# Revit family: Hager-VOLTA-Flush_mounted-IP30-With_Cover-With_DIN-Hosted-DE-de
name_source: partatom
category: Electrical Equipment
units: mm (PartAtom-declared; Revit-internal decimal feet)

## family parameters
Cut with Voids When Loaded = No
Host = Face
Maintain Annotation Orientation = Yes
Panel Configuration = Two Columns, Circuits Across
Part Type = Panelboard
Room Calculation Point = No
Round Connector Dimension = Use Diameter
Shared = No

## types (64) — shared parameters
BC_MODEL_ID = 1547151
BC_OBJECT_ID = 513474
BC_OBJECT_VERSION = #2
Code hager = ADD-EC000214_EU
EF000003 - Montageart = Unterputz
EF000008 - Breite = 348 mm  [stored 1.14173 ft]
EF000024 - UV-beständig = No
EF000116 - RAL-Nummer = 9010
EF001062 - EMV-Ausführung = No
EF001134 - DIN-Schiene = Yes
EF002950 - Breite in Teilungseinheiten = 12
EF005474 - Schutzart (IP) = IP30
EF006306 - Mit Schloss = No
ETIM class code = EC000214
ETIM class name = Small distribution board
HG000002-Mit tür = Yes
HG000003-Bereich = VOLTA
HG000005-Dicke = 2 mm  [stored 0.00656168 ft]
HG000006-Flush mounted = Yes
HG000009-Doppelflügeligen Tür = No
HG000010-Asymmetrische Türen = No
HG000012-Türschwenkwinkel = 90.00°
HG000013-Tür links = No
HG000014-Tür rechts = Yes
HG000015-Sichtbarkeit der Türöffnung = Yes
HG000016-3D-Türsichtbarkeit = Yes
HG000017-Distanz zwischen den Polen = 18 mm  [stored 0.0590551 ft]
HG000060-RAL-number = 9010
HG000099-Onfly Template ID-de-DE = 507532
HGEF0002950-Breite in Teilungseinheiten = 12
Manufacturer = Hager
Name = VOLTA-Flush_mounted-IP30-With_Cover-With_DIN-DE
Name BIM&CO = Electricity
Name hager = ADD_Enclosures_EC000214
Uniformat = Low Tension Service & Dist.
Uniformat code = D501001
zero-valued in all types: Default Elevation, EF001131 - Innentiefe, HG000007-Anzahl der leeren Spalten

## per-type parameters (varying)
| type | BC_VARIANT_ID | EF000007 - Farbe | EF000040 - Höhe | EF000049 - Tiefe | EF000118 - Mit Montageplatte | EF000218 - Einbautiefe | EF000266 - Anzahl der Reihen | EF000332 - Einbauhöhe | EF000846 - Einbaubreite | EF001088 - Anbaumöglichkeit | EF004462 - Art der Schließung | EF006244 - Transparenter Deckel/Tür | EF009212 - Ausführung Deckel | EF015776 - Erdungsklemmenblock | EF015777 - Neutralleiterklemmenblock | EF015941 - Signaldurchlassende Tür | HG000001-Anzahl der Spalten | HG000004-Herstellerreferenz | HG000008-Anzahl der leeren Reihen | HG000011-Leere Reihen von unten | HGEF000266-Anzahl der Reihen |
| VOLTA-Flush_mounted_W348_H356_D98_12_Modular_Spacing-VU12AT | 1174115 | weiß | 356 mm  [stored 1.16798 ft] | 98 mm  [stored 0.321522 ft] | No | 89 mm  [stored 0.291995 ft] | 1 | 321 mm  [stored 1.05315 ft] | 315 mm | Yes | sonstige | No | mit Ausschnitt | Yes | Yes | No | 1 | VU12AT | 0 | No | 1 |
| VOLTA-Flush_mounted_W348_H356_D94_12_Modular_Spacing-VU12DKN | 1174116 | weiß | 356 mm  [stored 1.16798 ft] | 94 mm  [stored 0.308399 ft] | No | 90 mm  [stored 0.295276 ft] | 1 | 340 mm  [stored 1.11549 ft] | 335 mm  [stored 1.09908 ft] | Yes | sonstige | No | mit Ausschnitt | No | No | No | 1 | VU12DKN | 0 | No | 1 |
| VOLTA-Flush_mounted_W348_H356_D94_12_Modular_Spacing-VU12EP | 1174117 | weiß | 356 mm  [stored 1.16798 ft] | 94 mm  [stored 0.308399 ft] | No | 90 mm  [stored 0.295276 ft] | 1 | 321 mm  [stored 1.05315 ft] | 335 mm  [stored 1.09908 ft] | Yes | sonstige | No | mit Ausschnitt | Yes | No | No | 1 | VU12EP | 0 | No | 1 |
| VOLTA-Flush_mounted_W348_H356_D94_12_Modular_Spacing-VU12ET | 1174118 | weiß | 356 mm  [stored 1.16798 ft] | 94 mm  [stored 0.308399 ft] | No | 90 mm  [stored 0.295276 ft] | 1 | 321 mm  [stored 1.05315 ft] | 335 mm  [stored 1.09908 ft] | Yes | sonstige | Yes | mit Ausschnitt | Yes | No | No | 1 | VU12ET | 0 | No | 1 |
| VOLTA-Flush_mounted_W348_H356_D98_12_Modular_Spacing-VU12LN | 1174119 | weiß | 356 mm  [stored 1.16798 ft] | 98 mm  [stored 0.321522 ft] | Yes | 89 mm  [stored 0.291995 ft] | 1 | 321 mm  [stored 1.05315 ft] | 315 mm | Yes | sonstige | No | mit Ausschnitt | Yes | No | No | 1 | VU12LN | 0 | No | 1 |
| VOLTA-Flush_mounted_W348_H356_D98_12_Modular_Spacing-VU12NA | 1174120 | weiß | 356 mm  [stored 1.16798 ft] | 98 mm  [stored 0.321522 ft] | No | 89 mm  [stored 0.291995 ft] | 1 | 321 mm  [stored 1.05315 ft] | 315 mm | Yes | sonstige | No | mit Ausschnitt | Yes | No | No | 1 | VU12NA | 0 | No | 1 |
| VOLTA-Flush_mounted_W348_H356_D98_12_Modular_Spacing-VU12NC | 1174121 |  | 356 mm  [stored 1.16798 ft] | 98 mm  [stored 0.321522 ft] | No | 89 mm  [stored 0.291995 ft] | 1 | 321 mm  [stored 1.05315 ft] | 315 mm | No |  | No |  | No | No | No | 1 | VU12NC | 0 | No | 1 |
| VOLTA-Flush_mounted_W348_H356_D94_12_Modular_Spacing-VU12NG | 1174122 | weiß | 356 mm  [stored 1.16798 ft] | 94 mm  [stored 0.308399 ft] | No | 90 mm  [stored 0.295276 ft] | 1 | 340 mm  [stored 1.11549 ft] | 335 mm  [stored 1.09908 ft] | Yes | sonstige | Yes | mit Ausschnitt | Yes | Yes | No | 1 | VU12NG | 0 | No | 1 |
| VOLTA-Flush_mounted_W348_H356_D94_12_Modular_Spacing-VU12NP | 1174123 | weiß | 356 mm  [stored 1.16798 ft] | 94 mm  [stored 0.308399 ft] | No | 90 mm  [stored 0.295276 ft] | 1 | 340 mm  [stored 1.11549 ft] | 335 mm  [stored 1.09908 ft] | Yes | sonstige | No | mit Ausschnitt | Yes | Yes | No | 1 | VU12NP | 0 | No | 1 |
| VOLTA-Flush_mounted_W348_H356_D94_12_Modular_Spacing-VU12NR | 1174124 | weiß | 356 mm  [stored 1.16798 ft] | 94 mm  [stored 0.308399 ft] | No | 90 mm  [stored 0.295276 ft] | 1 | 340 mm  [stored 1.11549 ft] | 335 mm  [stored 1.09908 ft] | Yes | sonstige | No | mit Ausschnitt | Yes | No | No | 1 | VU12NR | 0 | No | 1 |
| VOLTA-Flush_mounted_W348_H356_D94_12_Modular_Spacing-VU12NSG | 1174125 | weiß | 356 mm  [stored 1.16798 ft] | 94 mm  [stored 0.308399 ft] | No | 90 mm  [stored 0.295276 ft] | 1 | 340 mm  [stored 1.11549 ft] | 335 mm  [stored 1.09908 ft] | Yes | sonstige | No | mit Ausschnitt | Yes | Yes | No | 1 | VU12NSG | 0 | No | 1 |
| VOLTA-Flush_mounted_W348_H356_D94_12_Modular_Spacing-VU12UA | 1174127 | weiß | 356 mm  [stored 1.16798 ft] | 94 mm  [stored 0.308399 ft] | No | 90 mm  [stored 0.295276 ft] | 1 | 340 mm  [stored 1.11549 ft] | 335 mm  [stored 1.09908 ft] | Yes | sonstige | No | mit Ausschnitt | No | No | No | 1 | VU12UA | 0 | No | 1 |
| VOLTA-Flush_mounted_W348_H505_D98_12_Modular_Spacing-VU24AT | 1174128 | weiß | 505 mm  [stored 1.65682 ft] | 98 mm  [stored 0.321522 ft] | No | 89 mm  [stored 0.291995 ft] | 2 | 470 mm  [stored 1.54199 ft] | 315 mm | Yes | sonstige | No | mit Ausschnitt | Yes | Yes | No | 1 | VU24AT | 0 | No | 2 |
| VOLTA-Flush_mounted_W348_H505_D94_12_Modular_Spacing-VU24DKN | 1174129 | weiß | 505 mm  [stored 1.65682 ft] | 94 mm  [stored 0.308399 ft] | No | 90 mm  [stored 0.295276 ft] | 2 | 490 mm  [stored 1.60761 ft] | 335 mm  [stored 1.09908 ft] | Yes | sonstige | No | mit Ausschnitt | No | No | No | 1 | VU24DKN | 0 | No | 2 |
| VOLTA-Flush_mounted_W348_H505_D94_12_Modular_Spacing-VU24EP | 1174130 | weiß | 505 mm  [stored 1.65682 ft] | 94 mm  [stored 0.308399 ft] | No | 90 mm  [stored 0.295276 ft] | 2 | 471 mm  [stored 1.54528 ft] | 335 mm  [stored 1.09908 ft] | Yes | sonstige | No | mit Ausschnitt | Yes | No | No | 1 | VU24EP | 0 | No | 2 |
| VOLTA-Flush_mounted_W348_H505_D94_12_Modular_Spacing-VU24ET | 1174132 | weiß | 505 mm  [stored 1.65682 ft] | 94 mm  [stored 0.308399 ft] | No | 90 mm  [stored 0.295276 ft] | 2 | 471 mm  [stored 1.54528 ft] | 335 mm  [stored 1.09908 ft] | Yes | sonstige | Yes | mit Ausschnitt | Yes | No | No | 1 | VU24ET | 0 | No | 2 |
| VOLTA-Flush_mounted_W348_H505_D98_12_Modular_Spacing-VU24LN | 1174133 | weiß | 505 mm  [stored 1.65682 ft] | 98 mm  [stored 0.321522 ft] | Yes | 89 mm  [stored 0.291995 ft] | 2 | 470 mm  [stored 1.54199 ft] | 315 mm | Yes | sonstige | No | mit Ausschnitt | Yes | No | No | 1 | VU24LN | 0 | No | 2 |
| VOLTA-Flush_mounted_W348_H505_D98_12_Modular_Spacing-VU24NA | 1174134 | weiß | 505 mm  [stored 1.65682 ft] | 98 mm  [stored 0.321522 ft] | No | 89 mm  [stored 0.291995 ft] | 2 | 470 mm  [stored 1.54199 ft] | 315 mm | Yes | sonstige | No | mit Ausschnitt | Yes | No | No | 1 | VU24NA | 0 | No | 2 |
| VOLTA-Flush_mounted_W348_H505_D98_12_Modular_Spacing-VU24NC | 1174135 |  | 505 mm  [stored 1.65682 ft] | 98 mm  [stored 0.321522 ft] | No | 89 mm  [stored 0.291995 ft] | 2 | 470 mm  [stored 1.54199 ft] | 315 mm | No |  | No |  | No | No | No | 1 | VU24NC | 0 | No | 2 |
| VOLTA-Flush_mounted_W348_H505_D94_12_Modular_Spacing-VU24NG | 1174137 | weiß | 505 mm  [stored 1.65682 ft] | 94 mm  [stored 0.308399 ft] | No | 90 mm  [stored 0.295276 ft] | 2 | 490 mm  [stored 1.60761 ft] | 335 mm  [stored 1.09908 ft] | Yes | sonstige | Yes | mit Ausschnitt | Yes | Yes | No | 1 | VU24NG | 0 | No | 2 |
| VOLTA-Flush_mounted_W348_H505_D94_12_Modular_Spacing-VU24NH | 1174138 | weiß | 505 mm  [stored 1.65682 ft] | 94 mm  [stored 0.308399 ft] | No | 90 mm  [stored 0.295276 ft] | 2 | 490 mm  [stored 1.60761 ft] | 335 mm  [stored 1.09908 ft] | Yes | sonstige | No | mit Ausschnitt | Yes | Yes | No | 1 | VU24NH | 0 | No | 2 |
| VOLTA-Flush_mounted_W348_H505_D94_12_Modular_Spacing-VU24NN | 1174139 | weiß | 505 mm  [stored 1.65682 ft] | 94 mm  [stored 0.308399 ft] | No | 90 mm  [stored 0.295276 ft] | 2 | 470 mm  [stored 1.54199 ft] | 335 mm  [stored 1.09908 ft] | Yes | sonstige | No | mit Ausschnitt | Yes | Yes | No | 1 | VU24NN | 0 | No | 2 |
| VOLTA-Flush_mounted_W348_H505_D94_12_Modular_Spacing-VU24NP | 1174141 | weiß | 505 mm  [stored 1.65682 ft] | 94 mm  [stored 0.308399 ft] | No | 90 mm  [stored 0.295276 ft] | 2 | 490 mm  [stored 1.60761 ft] | 335 mm  [stored 1.09908 ft] | Yes | sonstige | No | mit Ausschnitt | Yes | Yes | No | 1 | VU24NP | 0 | No | 2 |
| VOLTA-Flush_mounted_W348_H505_D94_12_Modular_Spacing-VU24NR | 1174142 | weiß | 505 mm  [stored 1.65682 ft] | 94 mm  [stored 0.308399 ft] | No | 90 mm  [stored 0.295276 ft] | 2 | 490 mm  [stored 1.60761 ft] | 335 mm  [stored 1.09908 ft] | Yes | sonstige | No | mit Ausschnitt | Yes | No | No | 1 | VU24NR | 0 | No | 2 |
| VOLTA-Flush_mounted_W348_H505_D94_12_Modular_Spacing-VU24NSG | 1174144 | weiß | 505 mm  [stored 1.65682 ft] | 94 mm  [stored 0.308399 ft] | No | 90 mm  [stored 0.295276 ft] | 2 | 490 mm  [stored 1.60761 ft] | 335 mm  [stored 1.09908 ft] | Yes | sonstige | No | mit Ausschnitt | Yes | Yes | No | 1 | VU24NSG | 0 | No | 2 |
| VOLTA-Flush_mounted_W348_H505_D94_12_Modular_Spacing-VU24UA | 1174145 | weiß | 505 mm  [stored 1.65682 ft] | 94 mm  [stored 0.308399 ft] | No | 90 mm  [stored 0.295276 ft] | 2 | 490 mm  [stored 1.60761 ft] | 335 mm  [stored 1.09908 ft] | Yes | sonstige | No | mit Ausschnitt | No | No | No | 1 | VU24UA | 0 | No | 2 |
| VOLTA-Flush_mounted_W348_H630_D98_12_Modular_Spacing-VU36AT | 1174146 | weiß | 630 mm  [stored 2.06693 ft] | 98 mm  [stored 0.321522 ft] | No | 89 mm  [stored 0.291995 ft] | 3 | 595 mm  [stored 1.9521 ft] | 315 mm | Yes | sonstige | No | mit Ausschnitt | Yes | Yes | No | 1 | VU36AT | 0 | No | 3 |
| VOLTA-Flush_mounted_W348_H630_D94_12_Modular_Spacing-VU36DKN | 1174147 | weiß | 630 mm  [stored 2.06693 ft] | 94 mm  [stored 0.308399 ft] | No | 90 mm  [stored 0.295276 ft] | 3 | 615 mm  [stored 2.01772 ft] | 335 mm  [stored 1.09908 ft] | Yes | sonstige | No | mit Ausschnitt | No | No | No | 1 | VU36DKN | 0 | No | 3 |
| VOLTA-Flush_mounted_W348_H630_D94_12_Modular_Spacing-VU36EP | 1174148 | weiß | 630 mm  [stored 2.06693 ft] | 94 mm  [stored 0.308399 ft] | No | 90 mm  [stored 0.295276 ft] | 3 | 596 mm  [stored 1.95538 ft] | 335 mm  [stored 1.09908 ft] | Yes | sonstige | No | mit Ausschnitt | Yes | No | No | 1 | VU36EP | 0 | No | 3 |
| VOLTA-Flush_mounted_W348_H630_D94_12_Modular_Spacing-VU36ET | 1174149 | weiß | 630 mm  [stored 2.06693 ft] | 94 mm  [stored 0.308399 ft] | No | 90 mm  [stored 0.295276 ft] | 3 | 596 mm  [stored 1.95538 ft] | 335 mm  [stored 1.09908 ft] | Yes | sonstige | Yes | mit Ausschnitt | Yes | No | No | 1 | VU36ET | 0 | No | 3 |
| VOLTA-Flush_mounted_W348_H630_D98_12_Modular_Spacing-VU36LN | 1174150 | weiß | 630 mm  [stored 2.06693 ft] | 98 mm  [stored 0.321522 ft] | Yes | 89 mm  [stored 0.291995 ft] | 3 | 595 mm  [stored 1.9521 ft] | 315 mm | Yes | sonstige | No | mit Ausschnitt | Yes | No | No | 1 | VU36LN | 0 | No | 3 |
| VOLTA-Flush_mounted_W348_H630_D98_12_Modular_Spacing-VU36NA | 1174151 | weiß | 630 mm  [stored 2.06693 ft] | 98 mm  [stored 0.321522 ft] | No | 89 mm  [stored 0.291995 ft] | 3 | 595 mm  [stored 1.9521 ft] | 315 mm | Yes | sonstige | No | mit Ausschnitt | Yes | No | No | 1 | VU36NA | 0 | No | 3 |
| VOLTA-Flush_mounted_W348_H630_D98_12_Modular_Spacing-VU36NC | 1174152 |  | 630 mm  [stored 2.06693 ft] | 98 mm  [stored 0.321522 ft] | No | 89 mm  [stored 0.291995 ft] | 3 | 595 mm  [stored 1.9521 ft] | 315 mm | No |  | No |  | No | No | No | 1 | VU36NC | 0 | No | 3 |
| VOLTA-Flush_mounted_W348_H630_D94_12_Modular_Spacing-VU36NCT | 1174153 | weiß | 630 mm  [stored 2.06693 ft] | 94 mm  [stored 0.308399 ft] | No | 90 mm  [stored 0.295276 ft] | 3 | 596 mm  [stored 1.95538 ft] | 335 mm  [stored 1.09908 ft] | Yes | sonstige | No | mit Ausschnitt | No | No | No | 1 | VU36NCT | 0 | No | 3 |
| VOLTA-Flush_mounted_W348_H630_D94_12_Modular_Spacing-VU36NG | 1174154 | weiß | 630 mm  [stored 2.06693 ft] | 94 mm  [stored 0.308399 ft] | No | 90 mm  [stored 0.295276 ft] | 3 | 615 mm  [stored 2.01772 ft] | 335 mm  [stored 1.09908 ft] | Yes | sonstige | Yes | mit Ausschnitt | Yes | Yes | No | 1 | VU36NG | 0 | No | 3 |
| VOLTA-Flush_mounted_W348_H630_D94_12_Modular_Spacing-VU36NH | 1174155 | weiß | 630 mm  [stored 2.06693 ft] | 94 mm  [stored 0.308399 ft] | No | 90 mm  [stored 0.295276 ft] | 3 | 615 mm  [stored 2.01772 ft] | 335 mm  [stored 1.09908 ft] | Yes | sonstige | No | mit Ausschnitt | Yes | Yes | No | 1 | VU36NH | 0 | No | 3 |
| VOLTA-Flush_mounted_W348_H630_D94_12_Modular_Spacing-VU36NN | 1174156 | weiß | 630 mm  [stored 2.06693 ft] | 94 mm  [stored 0.308399 ft] | No | 90 mm  [stored 0.295276 ft] | 3 | 595 mm  [stored 1.9521 ft] | 335 mm  [stored 1.09908 ft] | Yes | sonstige | No | mit Ausschnitt | Yes | Yes | No | 1 | VU36NN | 0 | No | 3 |
| VOLTA-Flush_mounted_W348_H630_D94_12_Modular_Spacing-VU36NP | 1174157 | weiß | 630 mm  [stored 2.06693 ft] | 94 mm  [stored 0.308399 ft] | No | 90 mm  [stored 0.295276 ft] | 3 | 615 mm  [stored 2.01772 ft] | 335 mm  [stored 1.09908 ft] | Yes | sonstige | No | mit Ausschnitt | Yes | Yes | No | 1 | VU36NP | 0 | No | 3 |
| VOLTA-Flush_mounted_W348_H630_D94_12_Modular_Spacing-VU36NR | 1174159 | weiß | 630 mm  [stored 2.06693 ft] | 94 mm  [stored 0.308399 ft] | No | 90 mm  [stored 0.295276 ft] | 3 | 615 mm  [stored 2.01772 ft] | 335 mm  [stored 1.09908 ft] | Yes | sonstige | No | mit Ausschnitt | Yes | No | No | 1 | VU36NR | 0 | No | 3 |
| VOLTA-Flush_mounted_W348_H630_D98_12_Modular_Spacing-VU36NRM | 1174160 | weiß | 630 mm  [stored 2.06693 ft] | 98 mm  [stored 0.321522 ft] | No | 89 mm  [stored 0.291995 ft] | 3 | 595 mm  [stored 1.9521 ft] | 315 mm | Yes | sonstige | No | mit Ausschnitt | No | No | Yes | 1 | VU36NRM | 0 | No | 3 |
| VOLTA-Flush_mounted_W348_H630_D94_12_Modular_Spacing-VU36NSG | 1174161 | weiß | 630 mm  [stored 2.06693 ft] | 94 mm  [stored 0.308399 ft] | No | 90 mm  [stored 0.295276 ft] | 3 | 615 mm  [stored 2.01772 ft] | 335 mm  [stored 1.09908 ft] | Yes | sonstige | No | mit Ausschnitt | Yes | Yes | No | 1 | VU36NSG | 0 | No | 3 |
| VOLTA-Flush_mounted_W348_H630_D94_12_Modular_Spacing-VU36UA | 1174162 | weiß | 630 mm  [stored 2.06693 ft] | 94 mm  [stored 0.308399 ft] | No | 90 mm  [stored 0.295276 ft] | 3 | 615 mm  [stored 2.01772 ft] | 335 mm  [stored 1.09908 ft] | Yes | sonstige | No | mit Ausschnitt | No | No | No | 1 | VU36UA | 0 | No | 3 |
| VOLTA-Flush_mounted_W348_H630_D98_12_Modular_Spacing-VU36WWH | 1174163 | weiß | 630 mm  [stored 2.06693 ft] | 98 mm  [stored 0.321522 ft] | Yes | 89 mm  [stored 0.291995 ft] | 0 | 595 mm  [stored 1.9521 ft] | 315 mm | Yes | sonstige | No | mit Ausschnitt | No | No | Yes | 0 | VU36WWH | 0 | No | 0 |
| VOLTA-Flush_mounted_W348_H755_D98_12_Modular_Spacing-VU48AT | 1174164 | weiß | 755 mm  [stored 2.47703 ft] | 98 mm  [stored 0.321522 ft] | No | 89 mm  [stored 0.291995 ft] | 4 | 720 mm  [stored 2.3622 ft] | 315 mm | Yes | sonstige | No | mit Ausschnitt | Yes | Yes | No | 1 | VU48AT | 0 | No | 4 |
| VOLTA-Flush_mounted_W348_H755_D94_12_Modular_Spacing-VU48DKN | 1174165 | weiß | 755 mm  [stored 2.47703 ft] | 94 mm  [stored 0.308399 ft] | No | 90 mm  [stored 0.295276 ft] | 4 | 740 mm  [stored 2.42782 ft] | 335 mm  [stored 1.09908 ft] | Yes | sonstige | No | mit Ausschnitt | No | No | No | 1 | VU48DKN | 0 | No | 4 |
| VOLTA-Flush_mounted_W348_H755_D94_12_Modular_Spacing-VU48EP | 1174166 | weiß | 755 mm  [stored 2.47703 ft] | 94 mm  [stored 0.308399 ft] | No | 90 mm  [stored 0.295276 ft] | 4 | 721 mm  [stored 2.36549 ft] | 335 mm  [stored 1.09908 ft] | Yes | sonstige | No | mit Ausschnitt | Yes | No | No | 1 | VU48EP | 0 | No | 4 |
| VOLTA-Flush_mounted_W348_H755_D94_12_Modular_Spacing-VU48ET | 1174167 | weiß | 755 mm  [stored 2.47703 ft] | 94 mm  [stored 0.308399 ft] | No | 90 mm  [stored 0.295276 ft] | 4 | 721 mm  [stored 2.36549 ft] | 335 mm  [stored 1.09908 ft] | Yes | sonstige | Yes | mit Ausschnitt | Yes | No | No | 1 | VU48ET | 0 | No | 4 |
| VOLTA-Flush_mounted_W348_H755_D98_12_Modular_Spacing-VU48LN | 1174168 | weiß | 755 mm  [stored 2.47703 ft] | 98 mm  [stored 0.321522 ft] | Yes | 89 mm  [stored 0.291995 ft] | 4 | 720 mm  [stored 2.3622 ft] | 315 mm | Yes | sonstige | No | mit Ausschnitt | Yes | No | No | 1 | VU48LN | 0 | No | 4 |
| VOLTA-Flush_mounted_W348_H755_D98_12_Modular_Spacing-VU48NA | 1174169 | weiß | 755 mm  [stored 2.47703 ft] | 98 mm  [stored 0.321522 ft] | No | 89 mm  [stored 0.291995 ft] | 4 | 720 mm  [stored 2.3622 ft] | 315 mm | Yes | sonstige | No | mit Ausschnitt | Yes | No | No | 1 | VU48NA | 0 | No | 4 |
| VOLTA-Flush_mounted_W348_H755_D98_12_Modular_Spacing-VU48NC | 1174170 |  | 755 mm  [stored 2.47703 ft] | 98 mm  [stored 0.321522 ft] | No | 89 mm  [stored 0.291995 ft] | 4 | 720 mm  [stored 2.3622 ft] | 315 mm | No |  | No |  | No | No | No | 1 | VU48NC | 0 | No | 4 |
| VOLTA-Flush_mounted_W348_H755_D94_12_Modular_Spacing-VU48NCT | 1174171 | weiß | 755 mm  [stored 2.47703 ft] | 94 mm  [stored 0.308399 ft] | No | 90 mm  [stored 0.295276 ft] | 0 | 721 mm  [stored 2.36549 ft] | 335 mm  [stored 1.09908 ft] | Yes | sonstige | No | mit Ausschnitt | No | No | No | 1 | VU48NCT | 0 | No | 0 |
| VOLTA-Flush_mounted_W348_H755_D94_12_Modular_Spacing-VU48NG | 1174172 | weiß | 755 mm  [stored 2.47703 ft] | 94 mm  [stored 0.308399 ft] | No | 90 mm  [stored 0.295276 ft] | 4 | 740 mm  [stored 2.42782 ft] | 335 mm  [stored 1.09908 ft] | Yes | sonstige | Yes | mit Ausschnitt | Yes | Yes | No | 1 | VU48NG | 0 | No | 4 |
| VOLTA-Flush_mounted_W348_H755_D94_12_Modular_Spacing-VU48NH | 1174173 | weiß | 755 mm  [stored 2.47703 ft] | 94 mm  [stored 0.308399 ft] | No | 90 mm  [stored 0.295276 ft] | 4 | 740 mm  [stored 2.42782 ft] | 335 mm  [stored 1.09908 ft] | Yes | sonstige | No | mit Ausschnitt | Yes | Yes | No | 1 | VU48NH | 0 | No | 4 |
| VOLTA-Flush_mounted_W348_H755_D94_12_Modular_Spacing-VU48NP | 1174174 | weiß | 755 mm  [stored 2.47703 ft] | 94 mm  [stored 0.308399 ft] | No | 90 mm  [stored 0.295276 ft] | 4 | 740 mm  [stored 2.42782 ft] | 335 mm  [stored 1.09908 ft] | Yes | sonstige | No | mit Ausschnitt | Yes | Yes | No | 1 | VU48NP | 0 | No | 4 |
| VOLTA-Flush_mounted_W348_H755_D94_12_Modular_Spacing-VU48NR | 1174175 | weiß | 755 mm  [stored 2.47703 ft] | 94 mm  [stored 0.308399 ft] | No | 90 mm  [stored 0.295276 ft] | 0 | 740 mm  [stored 2.42782 ft] | 335 mm  [stored 1.09908 ft] | Yes | sonstige | No | mit Ausschnitt | Yes | No | No | 1 | VU48NR | 0 | Yes | 0 |
| VOLTA-Flush_mounted_W348_H755_D98_12_Modular_Spacing-VU48NRM | 1174176 |  | 755 mm  [stored 2.47703 ft] | 98 mm  [stored 0.321522 ft] | No | 89 mm  [stored 0.291995 ft] | 4 | 720 mm  [stored 2.3622 ft] | 315 mm | No |  | No |  | No | No | No | 1 | VU48NRM | 0 | No | 4 |
| VOLTA-Flush_mounted_W348_H755_D94_12_Modular_Spacing-VU48NSG | 1174177 | weiß | 755 mm  [stored 2.47703 ft] | 94 mm  [stored 0.308399 ft] | No | 90 mm  [stored 0.295276 ft] | 4 | 740 mm  [stored 2.42782 ft] | 335 mm  [stored 1.09908 ft] | Yes | sonstige | No | mit Ausschnitt | Yes | Yes | No | 1 | VU48NSG | 0 | No | 4 |
| VOLTA-Flush_mounted_W348_H755_D94_12_Modular_Spacing-VU48UA | 1174178 | weiß | 755 mm  [stored 2.47703 ft] | 94 mm  [stored 0.308399 ft] | No | 90 mm  [stored 0.295276 ft] | 4 | 740 mm  [stored 2.42782 ft] | 335 mm  [stored 1.09908 ft] | Yes | sonstige | No | mit Ausschnitt | No | No | No | 1 | VU48UA | 0 | No | 4 |
| VOLTA-Flush_mounted_W348_H880_D98_12_Modular_Spacing-VU602NWH | 1174179 |  | 880 mm  [stored 2.88714 ft] | 98 mm  [stored 0.321522 ft] | No | 89 mm  [stored 0.291995 ft] | 6 | 865 mm  [stored 2.83793 ft] | 315 mm | No |  | No |  | No | No | No | 1 | VU602NWH | 4 | Yes | 6 |
| VOLTA-Flush_mounted_W348_H880_D98_12_Modular_Spacing-VU602WWH | 1174180 |  | 880 mm  [stored 2.88714 ft] | 98 mm  [stored 0.321522 ft] | No | 89 mm  [stored 0.291995 ft] | 6 | 865 mm  [stored 2.83793 ft] | 315 mm | No |  | No |  | No | No | No | 1 | VU602WWH | 4 | Yes | 6 |
| VOLTA-Flush_mounted_W348_H880_D98_12_Modular_Spacing-VU603NWH | 1174181 |  | 880 mm  [stored 2.88714 ft] | 98 mm  [stored 0.321522 ft] | No | 89 mm  [stored 0.291995 ft] | 6 | 865 mm  [stored 2.83793 ft] | 315 mm | No |  | No |  | No | No | No | 1 | VU603NWH | 3 | Yes | 6 |
| VOLTA-Flush_mounted_W348_H880_D98_12_Modular_Spacing-VU603WWH | 1174182 |  | 880 mm  [stored 2.88714 ft] | 98 mm  [stored 0.321522 ft] | No | 89 mm  [stored 0.291995 ft] | 6 | 865 mm  [stored 2.83793 ft] | 315 mm | No |  | No |  | No | No | No | 1 | VU603WWH | 3 | Yes | 6 |
| VOLTA-Flush_mounted_W348_H880_D98_12_Modular_Spacing-VU60AT | 1174183 | weiß | 880 mm  [stored 2.88714 ft] | 98 mm  [stored 0.321522 ft] | No | 89 mm  [stored 0.291995 ft] | 5 | 845 mm  [stored 2.77231 ft] | 315 mm | Yes | sonstige | No | mit Ausschnitt | Yes | Yes | No | 1 | VU60AT | 0 | No | 5 |
| VOLTA-Flush_mounted_W348_H880_D98_12_Modular_Spacing-VU60NC | 1174184 | weiß | 880 mm  [stored 2.88714 ft] | 98 mm  [stored 0.321522 ft] | No | 89 mm  [stored 0.291995 ft] | 5 | 846 mm  [stored 2.77559 ft] | 315 mm | Yes | sonstige | No | mit Ausschnitt | Yes | No | No | 1 | VU60NC | 0 | No | 5 |

note: column(s) folded — value = type name in every type: Reference

note: [stored X ft] marks values corroborated as IEEE doubles in the binary element streams (Revit-internal decimal feet)

## geometry (parser evidence)
native form markers: Sweep x16
no freeform markers — native parametric forms only
